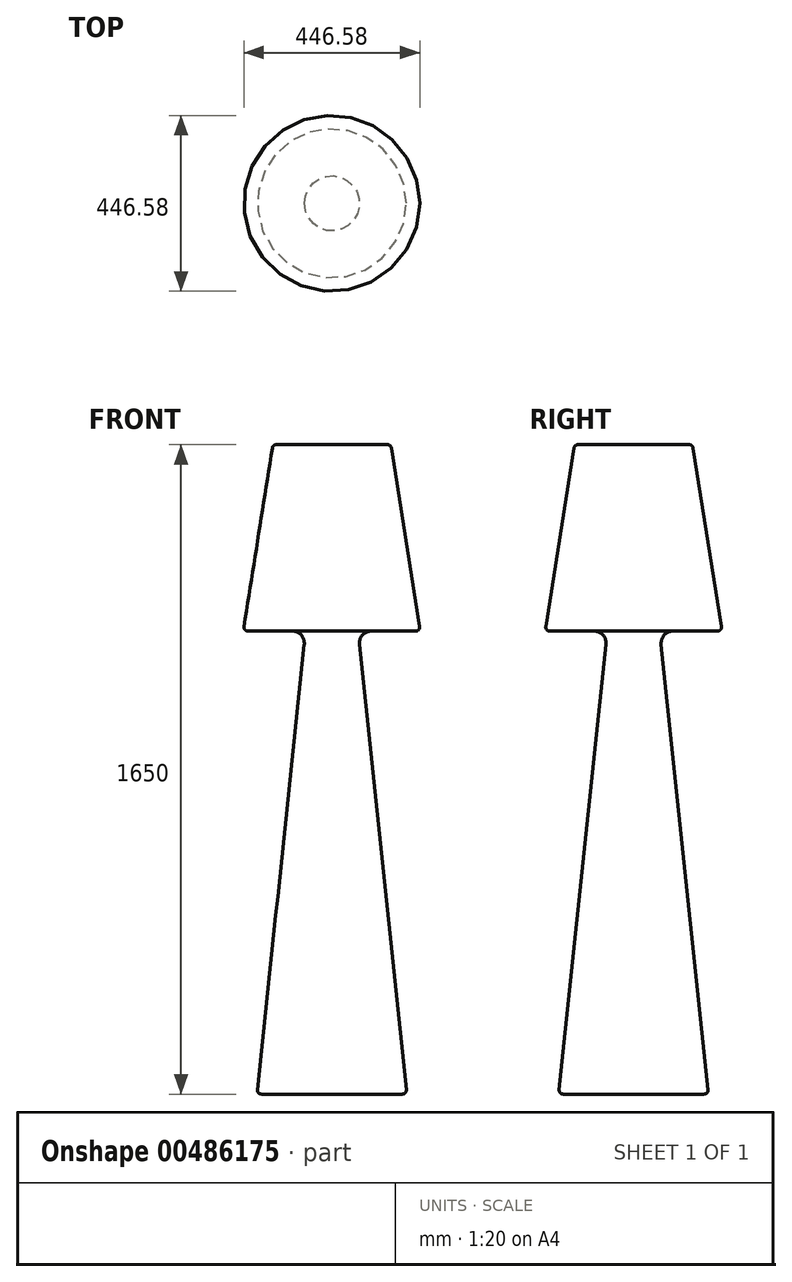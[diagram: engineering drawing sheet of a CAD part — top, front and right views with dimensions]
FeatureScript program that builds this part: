
annotation { "Feature Type Name" : "Feature", "Feature Type Description" : "" }
export const myFeature = defineFeature(function(context is Context, id is Id, definition is map)
    precondition{}
    {
        {
            var Q0;
            Q0=qCreatedBy(makeId("Front.planeOp"),FACE);
            var sketch = newSketch(context, id + "F0", { "sketchPlane" : qUnion([Q0])});
            skLineSegment(sketch, "E0", {"start": v(0, 0) * mm, "end": v(0, 1650) * mm, "construction": true});
            skLineSegment(sketch, "E1", {"start": v(-225, 1650) * mm, "end": v(225, 1650) * mm});
            skLineSegment(sketch, "E2", {"start": v(0, 1650) * mm, "end": v(-150, 1650) * mm});
            skLineSegment(sketch, "E3", {"start": v(-150, 1650) * mm, "end": v(-225, 1176.47) * mm});
            skLineSegment(sketch, "E4", {"start": v(-225, 1176.47) * mm, "end": v(-75, 1176.47) * mm});
            skLineSegment(sketch, "E5", {"start": v(-75, 1176.47) * mm, "end": v(-69.71, 1146.47) * mm});
            skLineSegment(sketch, "E6", {"start": v(-69.71, 1146.47) * mm, "end": v(-190.2, 0) * mm});
            skLineSegment(sketch, "E7", {"start": v(-190.2, 0) * mm, "end": v(0, 0) * mm});
            skLineSegment(sketch, "E8", {"start": v(0, 0) * mm, "end": v(0, 1650) * mm});
            skSolve(sketch);
        }
        {
            var Q0;
            Q0 = qSketchRegion(id + "F0", true);
            var Q1;
            Q1=sQuery(id+"F0.wireOp",EDGE,"E8");
            revolve(context, id + "F1", {"entities" : qUnion([Q0]), "axis" : qUnion([Q1]), "revolveType" : RevolveType.FULL});
        }
        {
            var Q0;
            Q0=makeQuery(id+"F1.opRevolve","SWEPT_EDGE",EDGE,{"disambiguationData":[OSD([sQuery(id+"F0.wireOp",EDGE,"E2"),sQuery(id+"F0.wireOp",EDGE,"E3")])]});
            var Q1;
            Q1=makeQuery(id+"F1.opRevolve","SWEPT_EDGE",EDGE,{"disambiguationData":[OSD([sQuery(id+"F0.wireOp",EDGE,"E3"),sQuery(id+"F0.wireOp",EDGE,"E4")])]});
            var Q2;
            Q2=makeQuery(id+"F1.opRevolve","SWEPT_EDGE",EDGE,{"disambiguationData":[OSD([sQuery(id+"F0.wireOp",EDGE,"E6"),sQuery(id+"F0.wireOp",EDGE,"E7")])]});
            fillet(context, id + "F2", {"entities" : qUnion([Q0, Q1, Q2]), "radius" : 10 * mm, "tangentPropagation" : true, "allowEdgeOverflow" : false});
        }
        {
            var Q0;
            Q0=makeQuery(id+"F1.opRevolve","SWEPT_EDGE",EDGE,{"disambiguationData":[OSD([sQuery(id+"F0.wireOp",EDGE,"E4"),sQuery(id+"F0.wireOp",EDGE,"E5")])]});
            var Q1;
            Q1=makeQuery(id+"F1.opRevolve","SWEPT_EDGE",EDGE,{"disambiguationData":[OSD([sQuery(id+"F0.wireOp",EDGE,"E5"),sQuery(id+"F0.wireOp",EDGE,"E6")])]});
            fillet(context, id + "F3", {"entities" : qUnion([Q0, Q1]), "radius" : 30 * mm, "tangentPropagation" : true, "allowEdgeOverflow" : false});
        }
    });
